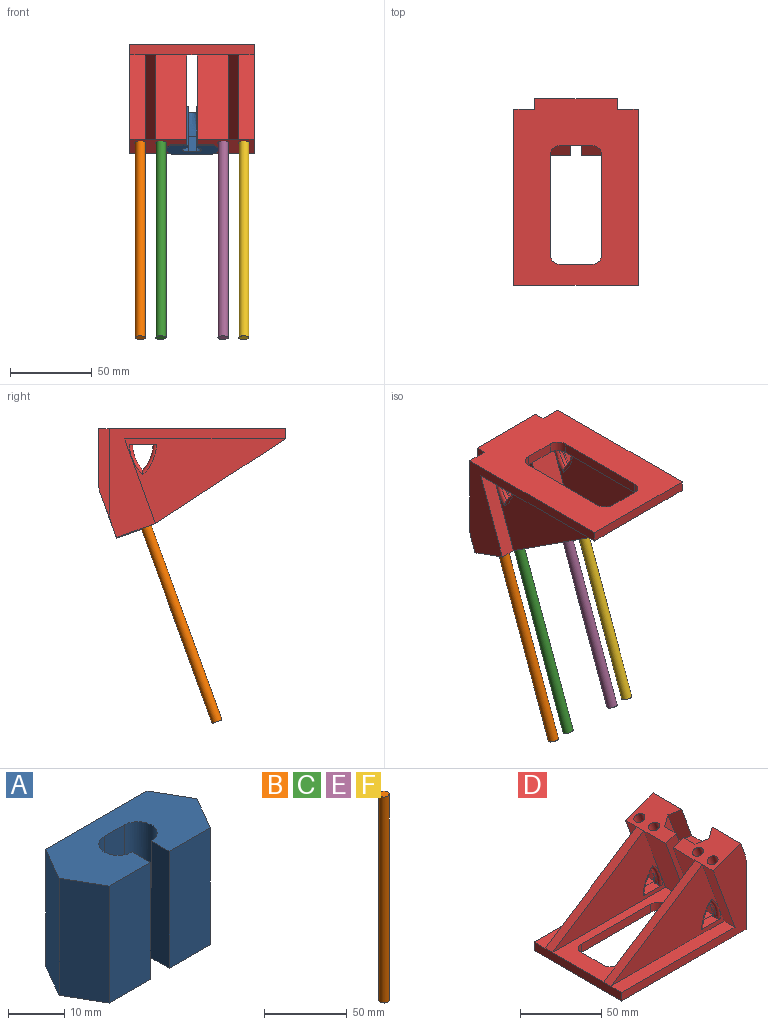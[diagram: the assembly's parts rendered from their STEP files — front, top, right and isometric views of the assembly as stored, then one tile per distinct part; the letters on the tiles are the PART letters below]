
ASSEMBLY  parts=6 mates=5
PART A: 19 faces, bbox 34.6x15.9x25.4 mm
  f0: cylinder r=3.17mm len=8.59mm, axis (0,0,1), area 13.4mm2, adj f10,f18
  f1: cylinder r=3.17mm len=8.59mm, axis (0,0,1), area 13.4mm2, adj f10,f18
  f2: plane 25.4x10.32mm, normal (0,-1,0), area 262.1mm2, adj f5,f9,f10,f11
  f3: plane 25.4x25.4mm, normal (0,1,0), area 645.2mm2, adj f4,f8,f9,f10
  f4: plane 25.4x7.94mm, normal (-0.87,0.5,0), area 232.8mm2, adj f3,f5,f9,f10
  f5: plane 25.4x7.94mm, normal (-0.87,-0.5,0), area 232.8mm2, adj f2,f4,f9,f10
  f6: plane 25.4x10.32mm, normal (0,-1,0), area 262.1mm2, adj f7,f9,f10,f12
  f7: plane 25.4x7.94mm, normal (0.87,-0.5,0), area 232.8mm2, adj f6,f8,f9,f10
  f8: plane 25.4x7.94mm, normal (0.87,0.5,0), area 232.8mm2, adj f3,f7,f9,f10
  f9: plane 34.57x15.88mm, normal (0,0,1), area 383.7mm2, adj f2,f3,f4,f5,f6,f7,f8,f11
  f10: plane 34.58x15.89mm, normal (0,0,-1), area 420mm2, adj f0,f1,f2,f3,f4,f5,f6,f7
  f11: plane 25.4x5.84mm, normal (1,0,0), area 124.8mm2, adj f2,f9,f10,f13,f18
  f12: plane 25.4x5.84mm, normal (-1,0,0), area 124.8mm2, adj f6,f9,f10,f14,f18
  f13: plane 10.01x0.11mm, normal (0,1,0), area 0.9mm2, adj f9,f11,f15,f18
  f14: plane 10.01x0.11mm, normal (0,1,0), area 0.9mm2, adj f9,f12,f16,f18
  f15: cylinder r=3.43mm len=10mm, axis (0,0,1), area 107.6mm2, adj f9,f13,f17,f18
  f16: cylinder r=3.43mm len=10mm, axis (0,0,1), area 107.6mm2, adj f9,f14,f17,f18
  f17: plane 10x4.95mm, normal (0,-1,0), area 49.5mm2, adj f9,f15,f16,f18
  f18: bspline ~15.4x11.76mm, area 278.8mm2, adj f0,f1,f10,f11,f12,f13,f14,f15
PART B: 3 faces, bbox 6.4x6.4x152.4 mm
  f0: cylinder r=3.17mm len=152.4mm, axis (0,0,-1), area 3040.2mm2, adj f1,f2
  f1: plane 6.35x6.35mm, normal (0,0,1), area 31.7mm2, adj f0
  f2: plane 6.35x6.35mm, normal (0,0,-1), area 31.7mm2, adj f0
PART C: same geometry as B
PART D: 74 faces, bbox 114.3x76.2x66.8 mm
  f0: plane 98.4x51.72mm, normal (0,-1,0), area 2332.1mm2, adj f15,f38,f42,f65,f72,f73
  f1: plane 98.4x51.72mm, normal (0,1,0), area 2332.1mm2, adj f4,f8,f42,f65,f66,f67
  f2: plane 98.4x51.72mm, normal (0,1,0), area 2332.1mm2, adj f7,f31,f43,f60,f68,f69
  f3: plane 98.4x51.72mm, normal (0,-1,0), area 2332.1mm2, adj f4,f6,f43,f60,f70,f71
  f4: plane 114.3x44.45mm, normal (0,0,1), area 2191.7mm2, adj f1,f3,f6,f8,f11,f12,f13,f16
  f5: plane 114.3x76.2mm, normal (0,0,-1), area 6265.3mm2, adj f13,f16,f18,f19,f20,f21,f22,f23
  f6: plane 51.72x19.05mm, normal (-0.94,0,-0.34), area 1048.5mm2, adj f3,f4,f12,f17
  f7: plane 98.4x9.53mm, normal (0,0,1), area 937.2mm2, adj f2,f16,f19,f31
  f8: plane 51.72x19.05mm, normal (-0.94,0,-0.34), area 1048.5mm2, adj f1,f4,f9,f11
  f9: plane 34.93x23.87mm, normal (-0.34,0,0.94), area 615.7mm2, adj f8,f10,f11,f18,f27,f28,f36,f37
  f10: plane 34.93x27.73mm, normal (0.94,0,0.34), area 540.2mm2, adj f9,f11,f18,f22,f28,f29,f52,f54
  f11: plane 54.98x34.73mm, normal (0,1,0), area 941.8mm2, adj f4,f8,f9,f10,f13,f29,f36,f54
  f12: plane 54.98x34.73mm, normal (0,-1,0), area 941.8mm2, adj f4,f6,f13,f14,f17,f24,f30,f50
  f13: plane 50.8x34.68mm, normal (1,0,0), area 1582mm2, adj f4,f5,f11,f12,f20,f22,f50,f54
  f14: plane 34.93x27.73mm, normal (0.94,0,0.34), area 540.2mm2, adj f12,f17,f19,f20,f24,f26,f50,f53
  f15: plane 98.4x9.53mm, normal (0,0,1), area 937.2mm2, adj f0,f16,f18,f38
  f16: plane 76.2x6.35mm, normal (-1,0,0), area 483.9mm2, adj f4,f5,f7,f15,f18,f19,f42,f43
  f17: plane 34.93x23.87mm, normal (-0.34,0,0.94), area 615.7mm2, adj f6,f12,f14,f19,f25,f26,f30,f31
  f18: plane 107.95x66.76mm, normal (0,-1,0), area 1781mm2, adj f5,f9,f10,f15,f16,f23,f38,f52
  f19: plane 107.95x66.76mm, normal (0,1,0), area 1781mm2, adj f5,f7,f14,f16,f17,f21,f31,f53
  f20: plane 56.47x7.12mm, normal (0,1,0), area 289.9mm2, adj f5,f13,f14,f21,f50,f53
  f21: plane 52.13x12.7mm, normal (1,0,0), area 662mm2, adj f5,f19,f20,f53
  f22: plane 56.47x7.12mm, normal (0,-1,0), area 289.9mm2, adj f5,f10,f13,f23,f52,f54
  f23: plane 52.13x12.7mm, normal (1,0,0), area 662mm2, adj f5,f18,f22,f52
  f24: plane 14.92x14.61mm, normal (-0.34,0,0.94), area 195.5mm2, adj f12,f14,f25,f26,f30
  f25: plane 26.58x16.15mm, normal (0.47,-0.87,0.17), area 232.8mm2, adj f17,f24,f26,f30
  f26: plane 26.58x16.15mm, normal (-0.47,-0.87,-0.17), area 232.8mm2, adj f14,f17,f24,f25
  f27: plane 26.58x16.15mm, normal (0.47,0.87,0.17), area 232.8mm2, adj f9,f28,f29,f36
  f28: plane 26.58x16.15mm, normal (-0.47,0.87,-0.17), area 232.8mm2, adj f9,f10,f27,f29
  f29: plane 14.92x14.61mm, normal (-0.34,0,0.94), area 195.5mm2, adj f10,f11,f27,f28,f36
  f30: plane 23.87x10.03mm, normal (0.94,0,0.34), area 254.6mm2, adj f12,f17,f24,f25
  f31: plane 51.72x18.82mm, normal (-0.94,0,-0.34), area 524.3mm2, adj f2,f7,f17,f19
  f32: cylinder r=3.47mm len=49.71mm, axis (-0.34,0,0.94), area 992.9mm2, adj f17,f34,f51
  f33: cylinder r=3.47mm len=49.71mm, axis (-0.34,0,0.94), area 992.9mm2, adj f17,f35,f49
  f34: plane 6.42x6.28mm, normal (-1,0,0), area 29.1mm2, adj f32,f51
  f35: plane 6.42x6.28mm, normal (-1,0,0), area 29.1mm2, adj f33,f49
  f36: plane 23.87x10.03mm, normal (0.94,0,0.34), area 254.6mm2, adj f9,f11,f27,f29
  f37: cylinder r=3.47mm len=49.71mm, axis (-0.34,0,0.94), area 992.9mm2, adj f9,f40,f48
  f38: plane 51.72x18.82mm, normal (-0.94,0,-0.34), area 524.3mm2, adj f0,f9,f15,f18
  f39: cylinder r=3.47mm len=49.71mm, axis (-0.34,0,0.94), area 992.9mm2, adj f9,f41,f55
  f40: plane 6.42x6.28mm, normal (-1,0,0), area 29.1mm2, adj f37,f48
  f41: plane 6.42x6.28mm, normal (-1,0,0), area 29.1mm2, adj f39,f55
  f42: plane 79.57x51.72mm, normal (-0.54,0,0.84), area 602.6mm2, adj f0,f1,f9,f16
  f43: plane 79.57x51.72mm, normal (-0.54,0,0.84), area 602.6mm2, adj f2,f3,f16,f17
  f44: plane 60.3x6.35mm, normal (0,-1,0), area 382.9mm2, adj f4,f5,f56,f59
  f45: plane 19.05x6.35mm, normal (1,0,0), area 121mm2, adj f4,f5,f56,f57
  f46: plane 60.3x6.35mm, normal (0,1,0), area 382.9mm2, adj f4,f5,f57,f58
  f47: plane 19.05x6.35mm, normal (-1,0,0), area 121mm2, adj f4,f5,f58,f59
  f48: cylinder r=12.7mm len=7.44mm, axis (0,-1,0), area 48mm2, adj f37,f40
  f49: cylinder r=12.7mm len=7.44mm, axis (0,-1,0), area 48mm2, adj f33,f35
  f50: cylinder r=12.7mm len=22.23mm, axis (0,1,0), area 98.5mm2, adj f12,f13,f14,f20
  f51: cylinder r=12.7mm len=7.44mm, axis (0,-1,0), area 48mm2, adj f32,f34
  f52: cylinder r=12.7mm len=12.7mm, axis (0,1,0), area 56.3mm2, adj f10,f18,f22,f23
  f53: cylinder r=12.7mm len=12.7mm, axis (0,1,0), area 56.3mm2, adj f14,f19,f20,f21
  f54: cylinder r=12.7mm len=22.23mm, axis (0,1,0), area 98.5mm2, adj f10,f11,f13,f22
  f55: cylinder r=12.7mm len=7.44mm, axis (0,-1,0), area 48mm2, adj f39,f41
  f56: cylinder r=6.35mm len=6.35mm, axis (0,0,1), area 63.3mm2, adj f4,f5,f44,f45
  f57: cylinder r=6.35mm len=6.35mm, axis (0,0,-1), area 63.3mm2, adj f4,f5,f45,f46
  f58: cylinder r=6.35mm len=6.35mm, axis (0,0,1), area 63.3mm2, adj f4,f5,f46,f47
  f59: cylinder r=6.35mm len=6.35mm, axis (0,0,-1), area 63.3mm2, adj f4,f5,f44,f47
  f60: plane 16.73x6.37mm, normal (0,0,1), area 84.1mm2, adj f2,f3,f61,f62,f68,f69,f70,f71
  f61: cylinder r=25mm len=15.88mm, axis (0,-1,0), area 41mm2, adj f60,f62,f68,f70
  f62: cylinder r=25mm len=15.88mm, axis (0,-1,0), area 41mm2, adj f60,f61,f69,f71
  f63: cylinder r=25mm len=15.88mm, axis (0,-1,0), area 41mm2, adj f64,f65,f67,f72
  f64: cylinder r=25mm len=15.88mm, axis (0,-1,0), area 41mm2, adj f63,f65,f66,f73
  f65: plane 16.73x6.37mm, normal (0,0,1), area 84.1mm2, adj f0,f1,f63,f64,f66,f67,f72,f73
  f66: torus R=27mm, axis (0,-1,0), area 59mm2, adj f1,f64,f65,f67
  f67: torus R=27mm, axis (0,-1,0), area 59mm2, adj f1,f63,f65,f66
  f68: torus R=27mm, axis (0,1,0), area 59mm2, adj f2,f60,f61,f69
  f69: torus R=27mm, axis (0,1,0), area 59mm2, adj f2,f60,f62,f68
  f70: torus R=27mm, axis (0,1,0), area 59mm2, adj f3,f60,f61,f71
  f71: torus R=27mm, axis (0,1,0), area 59mm2, adj f3,f60,f62,f70
  f72: torus R=27mm, axis (0,-1,0), area 59mm2, adj f0,f63,f65,f73
  f73: torus R=27mm, axis (0,-1,0), area 59mm2, adj f0,f64,f65,f72
PART E: same geometry as B
PART F: same geometry as B
PLACE A rot(axis=(0,0.98,-0.17),180deg) t=(0.09,45.87,-40.57)mm
PLACE B rot(axis=(-1,0,0),20deg) t=(-31.75,-16.88,-179.53)mm
PLACE C rot(axis=(-1,0,0),20deg) t=(-19.05,-16.88,-179.53)mm
PLACE D rot(axis=(-0.71,-0.71,0),180deg) t=(0,42.94,-6.35)mm
PLACE E rot(axis=(-1,0,0),20deg) t=(19.05,-16.88,-179.53)mm
PLACE F rot(axis=(-1,0,0),20deg) t=(31.75,-16.88,-179.53)mm
MATE fastened C.f0 <-> D.f37  axis (0,-0.34,-0.94) through (-19.05,35.24,-36.32)mm
MATE fastened E.f0 <-> D.f32  axis (0,0.34,0.94) through (19.05,35.24,-36.32)mm
MATE fastened B.f0 <-> D.f39  axis (0,0.34,0.94) through (-31.75,35.24,-36.32)mm
MATE planar D.f10 <-> A.f3  axis (0,0.94,-0.34) through (-21.66,49.34,-54.23)mm
MATE fastened F.f0 <-> D.f33  axis (0,0.34,0.94) through (31.75,35.24,-36.32)mm
